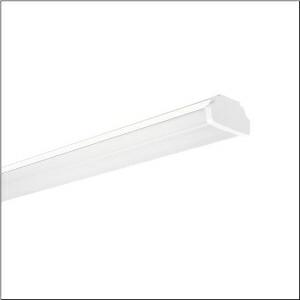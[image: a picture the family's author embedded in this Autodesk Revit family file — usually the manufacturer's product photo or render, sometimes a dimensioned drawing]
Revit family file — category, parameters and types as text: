
# Revit family: modario_r__31_ho_53bm812d2v4120_42ed
name_source: partatom
category: Lighting Fixtures
units: mm (PartAtom-declared; Revit-internal decimal feet)

## family parameters
Cut with Voids When Loaded = No
Host = Face
Light Source = No
Part Type = Normal
Room Calculation Point = No
Round Connector Dimension = Use Diameter
Shared = No

## types (1)
- --- (1 x LED, 12350 lm, 79.5 W, 4000K)
    Apparent Load = 80 VA
    CIE Flux Codes = 47 80 95 92 100
    Color Rendering = 80
    Color Temperature = 4000K
    Default Elevation = 1800 mm
    Description = Modario® 31 HOluminaire insert, length: 1.495mm, width: 81mm, height: 82mm, LED rated luminous flux: 12.350lm, light colour: 840, control gear: DALI 2, control gear: ECG DALI, with plug, 5-pole, with phase selection, mains connection: 220..240V, AC, 50/60Hz, primary optical cover: cover, of PMMA, light emission: direct distribution, primary light characteristic: symmetric, protection rating (complete): IP20, protection rating (LED compartment): IP50, insulation class (complete): insulation class I (protective earthing), certification: CE, ENEC, VDE, permissible ambient temperature for indoor applications: -25..+30°C, corresponds to IFS (International Featured Standards) requirements for safety and quality in the food industry, reducing of maximum allowable ambient temperature of 5°C with ceiling mounting, packaging unit: 1 piece
    Height = 92 mm
    Lamp = 1 x LED
    Lamp Light Flux = 12350 lm
    Lamp Power = 79.5 W
    Lamp count = 1
    Length = 1495 mm
    Luminous efficacy = 155 lm/W
    Manufacturer = Siteco
    ModVariant = No
    Model = 53BM812D2V4120
    Mounting Place = Ceiling
    Mounting Type = Pendant
    Number of Poles = 1
    OnlyDefault = Yes
    Power Factor = 1
    Product Name = Modario® 31 HO
    Product group = luminaire insert
    ProductGroupID = 902
    Protection Class = Protection class I
    Protection Degree = IP 20
    RLX_Detail_Level = 1
    RlxData = <blob elided: 42093 chars, md5=495154bd>
    Socket = socket
    Standby Power = 0 W
    System Light Flux = 12350 lm
    System Power = 80 W
    Type Comments = factory setting: luminous flux: 100 % | dim-lin: 254 | 345 mA
    Type Image = l_1003447.jpg
    URL = http://relux.com
    VarID = @adj_133603
    Voltage = 0 V
    Weight = 0.00 kg
    Width = 81 mm

## geometry (parser evidence)
native form markers: Blend x4, Sweep x12
no freeform markers — native parametric forms only
